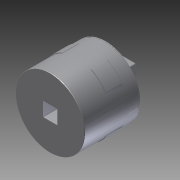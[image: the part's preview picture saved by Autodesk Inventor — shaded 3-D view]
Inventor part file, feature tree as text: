
AUTODESK INVENTOR PART (.ipt)
format: ipt  version: 2013 (Build 170138000, 138)  size: 280,064 bytes
history: native  units: mm
features: other x3, imported_body x2, sketch x1, extrude x1
ambient origin geometry x8: Origin, YZ Plane, XZ Plane, XY Plane, X Axis, Y Axis, Z Axis, Center Point
feature tree (7):
  parser-record x1  (decoder bookkeeping rows leaked as tree rows — omitted from the tree; the rows remain in map.json)
  imported_body  "Base1"
  imported_body  "Base2"
  other  "NONE_1"
  sketch  "Sketch1"  dims[d0=25.4mm d1=0.0mm d2=0.0mm]
  other  "Srf1"
  extrude  "ExtrusionSrf1"  TaperAngle=0.0deg  [1 undecoded]
note: 1 required parameter value undecoded (feature->parameter linkage not recoverable at this tier; creation-order binding heuristic only, values carry confidence <= 0.55)
